# Revit family: QF_BOURGEAT_NOMAD_Modèle_pour_liaison_froide
name_source: partatom
category: Equipement spécialisé
revit_build: Autodesk Revit 2015 (Build: 20140606_1530(x64)
units: mm (PartAtom-declared; Revit-internal decimal feet)

## types (12) — shared parameters
Fabricant = BOURGEAT
Fréquence = 50 Hz
Hauteur de porte bas = 409 mm
Hauteur de serrure bas = 172 mm  [stored 0.564304 ft]
Indice de protection = 21
Inox = Acier inoxydable, poli
Spécification du Fabricant = Modèle pour liaison froide
Type Fluide Frigorigène = R404a
URL catalogue = http://www.bourgeat.fr
Vitrage = Verre

## per-type parameters (varying)
- 2x4 avec pare-haleine - Dessus inox - neutre: 2x4=Oui; 2x8=Non; Capacité en bacs GN H.65 mm=2 x 4 GN1/1; Charge max=43.00 kg; Consommation énergétique=4.3KWh/h; Decalage porte=11 mm; Hauteur boitier de commande=128 mm  [stored 0.419948 ft]; Hauteur de porte haut=382 mm; Hauteur de serrure haut=160 mm  [stored 0.524934 ft]; Hauteur hors tout=1462 mm  [stored 4.79659 ft]; Hauteur plateau=1062 mm  [stored 3.48425 ft]; Intensité nominale=16 A; Longueur Pare haleine=897 mm  [stored 2.94291 ft]; Longueur hors tout=959 mm  [stored 3.14633 ft]; Modèle=887030; Nombre de repas=jusqu'à 30/40; Pare-haleine=Oui; Phase=2; Plaque Vitro 1=Non; Plaque vitro 2=Non; Poids net à vide=140.00 kg; Profondeur hors tout=795 mm  [stored 2.60827 ft]; Puissance frigorifique=450 W à -5°C; Puissance électrique =3800 W; Rampe=Non; Tension=230 V
- 2x4 avec pare-haleine - Dessus inox - neutre + lampe(s): 2x4=Oui; 2x8=Non; Capacité en bacs GN H.65 mm=2 x 4 GN1/1; Charge max=43.00 kg; Consommation énergétique=4.3KWh/h; Decalage porte=11 mm; Hauteur boitier de commande=128 mm  [stored 0.419948 ft]; Hauteur de porte haut=382 mm; Hauteur de serrure haut=160 mm  [stored 0.524934 ft]; Hauteur hors tout=1462 mm  [stored 4.79659 ft]; Hauteur plateau=1062 mm  [stored 3.48425 ft]; Intensité nominale=16 A; Longueur Pare haleine=897 mm  [stored 2.94291 ft]; Longueur hors tout=959 mm  [stored 3.14633 ft]; Modèle=887034; Nombre de repas=jusqu'à 30/40; Pare-haleine=Oui; Phase=2; Plaque Vitro 1=Non; Plaque vitro 2=Non; Poids net à vide=140.00 kg; Profondeur hors tout=795 mm  [stored 2.60827 ft]; Puissance frigorifique=450 W à-5°C; Puissance électrique =3800 W; Rampe=Non; Tension=230 V
- 2x4 avec pare-haleine - Dessus 1 plaque vitro + 1 lampe: 2x4=Oui; 2x8=Non; Capacité en bacs GN H.65 mm=2 x 4 GN1/1; Charge max=43.00 kg; Consommation énergétique=4.3KWh/h; Decalage porte=11 mm; Hauteur boitier de commande=128 mm  [stored 0.419948 ft]; Hauteur de porte haut=382 mm; Hauteur de serrure haut=160 mm  [stored 0.524934 ft]; Hauteur hors tout=1462 mm  [stored 4.79659 ft]; Hauteur plateau=1062 mm  [stored 3.48425 ft]; Intensité nominale=16 A; Longueur Pare haleine=897 mm  [stored 2.94291 ft]; Longueur hors tout=959 mm  [stored 3.14633 ft]; Modèle=887031; Nombre de repas=jusqu'à 30/40; Pare-haleine=Oui; Phase=2; Plaque Vitro 1=Oui; Plaque vitro 2=Non; Poids net à vide=140.00 kg; Profondeur hors tout=795 mm  [stored 2.60827 ft]; Puissance frigorifique=450 W à -5°C; Puissance électrique =3800 W; Rampe=Non; Tension=230 V
- 2x4 - Dessus inox - neutre: 2x4=Oui; 2x8=Non; Capacité en bacs GN H.65 mm=2 x 4 GN1/1; Charge max=60.00 kg; Consommation énergétique=4.3KWh/h; Decalage porte=11 mm; Hauteur boitier de commande=128 mm  [stored 0.419948 ft]; Hauteur de porte haut=382 mm; Hauteur de serrure haut=160 mm  [stored 0.524934 ft]; Hauteur hors tout=1174 mm  [stored 3.85171 ft]; Hauteur plateau=1062 mm  [stored 3.48425 ft]; Intensité nominale=16 A; Longueur Pare haleine=897 mm  [stored 2.94291 ft]; Longueur hors tout=959 mm  [stored 3.14633 ft]; Modèle=887130; Nombre de repas=jusqu'à 30/40; Pare-haleine=Non; Phase=2; Plaque Vitro 1=Non; Plaque vitro 2=Non; Poids net à vide=130.00 kg; Profondeur hors tout=791 mm; Puissance frigorifique=450 W à -5°C; Puissance électrique =3800 W; Rampe=Oui; Tension=230 V
- 2x4 - Dessus 1 plaque vitro + 1 lampe: 2x4=Oui; 2x8=Non; Capacité en bacs GN H.65 mm=2 x 4 GN1/1; Charge max=60.00 kg; Consommation énergétique=4.3KWh/h; Decalage porte=11 mm; Hauteur boitier de commande=128 mm  [stored 0.419948 ft]; Hauteur de porte haut=382 mm; Hauteur de serrure haut=160 mm  [stored 0.524934 ft]; Hauteur hors tout=1174 mm  [stored 3.85171 ft]; Hauteur plateau=1062 mm  [stored 3.48425 ft]; Intensité nominale=16 A; Longueur Pare haleine=897 mm  [stored 2.94291 ft]; Longueur hors tout=959 mm  [stored 3.14633 ft]; Modèle=887131; Nombre de repas=jusqu'à 30/40; Pare-haleine=Non; Phase=2; Plaque Vitro 1=Oui; Plaque vitro 2=Non; Poids net à vide=130.00 kg; Profondeur hors tout=791 mm; Puissance frigorifique=450 W à -5°C; Puissance électrique =3800 W; Rampe=Oui; Tension=230 V
- 2x8 avec pare-haleine - Dessus inox - neutre: 2x4=Non; 2x8=Oui; Capacité en bacs GN H.65 mm=2 x 8 GN1/1; Charge max=86.00 kg; Consommation énergétique=7.66KWh/h; Decalage porte=7 mm  [stored 0.0229659 ft]; Hauteur boitier de commande=35 mm  [stored 0.114829 ft]; Hauteur de porte haut=715 mm  [stored 2.3458 ft]; Hauteur de serrure haut=306 mm  [stored 1.00394 ft]; Hauteur hors tout=1371 mm  [stored 4.49803 ft]; Hauteur plateau=968 mm  [stored 3.17585 ft]; Intensité nominale=11 A; Longueur Pare haleine=1265 mm  [stored 4.15026 ft]; Longueur hors tout=1327 mm  [stored 4.35367 ft]; Modèle=887080; Nombre de repas=jusqu'à 60/80; Pare-haleine=Oui; Phase=3; Plaque Vitro 1=Non; Plaque vitro 2=Non; Poids net à vide=180.00 kg; Profondeur hors tout=795 mm  [stored 2.60827 ft]; Puissance frigorifique=450 W à -5°C; Puissance électrique =7000 W; Rampe=Non; Tension=400 V
- 2x8 avec pare-haleine - Dessus inox - neutre + lampe(s): 2x4=Non; 2x8=Oui; Capacité en bacs GN H.65 mm=2 x 8 GN1/1; Charge max=86.00 kg; Consommation énergétique=7.66KWh/h; Decalage porte=7 mm  [stored 0.0229659 ft]; Hauteur boitier de commande=35 mm  [stored 0.114829 ft]; Hauteur de porte haut=715 mm  [stored 2.3458 ft]; Hauteur de serrure haut=306 mm  [stored 1.00394 ft]; Hauteur hors tout=1371 mm  [stored 4.49803 ft]; Hauteur plateau=968 mm  [stored 3.17585 ft]; Intensité nominale=12 A; Longueur Pare haleine=1265 mm  [stored 4.15026 ft]; Longueur hors tout=1327 mm  [stored 4.35367 ft]; Modèle=887084; Nombre de repas=jusqu'à 60/80; Pare-haleine=Oui; Phase=3; Plaque Vitro 1=Non; Plaque vitro 2=Non; Poids net à vide=180.00 kg; Profondeur hors tout=795 mm  [stored 2.60827 ft]; Puissance frigorifique=450 W à -5°C; Puissance électrique =8000 W; Rampe=Non; Tension=400 V
- 2x8 avec pare-haleine - Dessus 1 plaque vitro + 1 lampe: 2x4=Non; 2x8=Oui; Capacité en bacs GN H.65 mm=2 x 8 GN1/1; Charge max=86.00 kg; Consommation énergétique=7.66KWh/h; Decalage porte=7 mm  [stored 0.0229659 ft]; Hauteur boitier de commande=35 mm  [stored 0.114829 ft]; Hauteur de porte haut=715 mm  [stored 2.3458 ft]; Hauteur de serrure haut=306 mm  [stored 1.00394 ft]; Hauteur hors tout=1371 mm  [stored 4.49803 ft]; Hauteur plateau=968 mm  [stored 3.17585 ft]; Intensité nominale=12 A; Longueur Pare haleine=1265 mm  [stored 4.15026 ft]; Longueur hors tout=1327 mm  [stored 4.35367 ft]; Modèle=887081; Nombre de repas=jusqu'à 60/80; Pare-haleine=Oui; Phase=3; Plaque Vitro 1=Oui; Plaque vitro 2=Non; Poids net à vide=180.00 kg; Profondeur hors tout=795 mm  [stored 2.60827 ft]; Puissance frigorifique=450 W à -5°C; Puissance électrique =7900 W; Rampe=Non; Tension=400 V
- 2x8 avec pare-haleine - Dessus 2 plaques vitro + 2 lampes: 2x4=Non; 2x8=Oui; Capacité en bacs GN H.65 mm=2 x 8 GN1/1; Charge max=86.00 kg; Consommation énergétique=7.66KWh/h; Decalage porte=7 mm  [stored 0.0229659 ft]; Hauteur boitier de commande=35 mm  [stored 0.114829 ft]; Hauteur de porte haut=715 mm  [stored 2.3458 ft]; Hauteur de serrure haut=306 mm  [stored 1.00394 ft]; Hauteur hors tout=1371 mm  [stored 4.49803 ft]; Hauteur plateau=968 mm  [stored 3.17585 ft]; Intensité nominale=13 A; Longueur Pare haleine=1265 mm  [stored 4.15026 ft]; Longueur hors tout=1327 mm  [stored 4.35367 ft]; Modèle=887082; Nombre de repas=jusqu'à 60/80; Pare-haleine=Oui; Phase=3; Plaque Vitro 1=Oui; Plaque vitro 2=Oui; Poids net à vide=180.00 kg; Profondeur hors tout=795 mm  [stored 2.60827 ft]; Puissance frigorifique=450 W 0 -5°C; Puissance électrique =8700 W; Rampe=Non; Tension=400 V
- 2x8 - Dessus inox - neutre: 2x4=Non; 2x8=Oui; Capacité en bacs GN H.65 mm=2 x 8 GN1/1; Charge max=86.00 kg; Consommation énergétique=7.66KWh/h; Decalage porte=7 mm  [stored 0.0229659 ft]; Hauteur boitier de commande=35 mm  [stored 0.114829 ft]; Hauteur de porte haut=715 mm  [stored 2.3458 ft]; Hauteur de serrure haut=306 mm  [stored 1.00394 ft]; Hauteur hors tout=1084 mm  [stored 3.55643 ft]; Hauteur plateau=968 mm  [stored 3.17585 ft]; Intensité nominale=11 A; Longueur Pare haleine=1265 mm  [stored 4.15026 ft]; Longueur hors tout=1327 mm  [stored 4.35367 ft]; Modèle=887180; Nombre de repas=jusqu'à 60/80; Pare-haleine=Non; Phase=3; Plaque Vitro 1=Non; Plaque vitro 2=Non; Poids net à vide=160.00 kg; Profondeur hors tout=795 mm  [stored 2.60827 ft]; Puissance frigorifique=450W à -5°C; Puissance électrique =7000 W; Rampe=Oui; Tension=400 V
- 2x8 - Dessus 1 plaque vitro + 1 lampe: 2x4=Non; 2x8=Oui; Capacité en bacs GN H.65 mm=2 x 8 GN1/1; Charge max=86.00 kg; Consommation énergétique=7.66KWh/h; Decalage porte=7 mm  [stored 0.0229659 ft]; Hauteur boitier de commande=35 mm  [stored 0.114829 ft]; Hauteur de porte haut=715 mm  [stored 2.3458 ft]; Hauteur de serrure haut=306 mm  [stored 1.00394 ft]; Hauteur hors tout=1084 mm  [stored 3.55643 ft]; Hauteur plateau=968 mm  [stored 3.17585 ft]; Intensité nominale=11 A; Longueur Pare haleine=1265 mm  [stored 4.15026 ft]; Longueur hors tout=1327 mm  [stored 4.35367 ft]; Modèle=887181; Nombre de repas=jusqu'à 60/80; Pare-haleine=Non; Phase=3; Plaque Vitro 1=Oui; Plaque vitro 2=Non; Poids net à vide=160.00 kg; Profondeur hors tout=795 mm  [stored 2.60827 ft]; Puissance frigorifique=450 W à -5°C; Puissance électrique =7400 W; Rampe=Oui; Tension=400 V
- 2x8 - Dessus 2 plaques vitro + 2 lampes: 2x4=Non; 2x8=Oui; Capacité en bacs GN H.65 mm=2 x 8 GN1/1; Charge max=86.00 kg; Consommation énergétique=7.66KWh/h; Decalage porte=7 mm  [stored 0.0229659 ft]; Hauteur boitier de commande=35 mm  [stored 0.114829 ft]; Hauteur de porte haut=715 mm  [stored 2.3458 ft]; Hauteur de serrure haut=306 mm  [stored 1.00394 ft]; Hauteur hors tout=1084 mm  [stored 3.55643 ft]; Hauteur plateau=968 mm  [stored 3.17585 ft]; Intensité nominale=11 A; Longueur Pare haleine=1265 mm  [stored 4.15026 ft]; Longueur hors tout=1327 mm  [stored 4.35367 ft]; Modèle=887182; Nombre de repas=jusqu'à 60/80; Pare-haleine=Non; Phase=3; Plaque Vitro 1=Oui; Plaque vitro 2=Oui; Poids net à vide=160.00 kg; Profondeur hors tout=795 mm  [stored 2.60827 ft]; Puissance frigorifique=450 W à -5°C; Puissance électrique =7700 W; Rampe=Oui; Tension=400 V

note: [stored X ft] marks values corroborated as IEEE doubles in the binary element streams (Revit-internal decimal feet)

## geometry (parser evidence)
native form markers: Blend x2
no freeform markers — native parametric forms only
